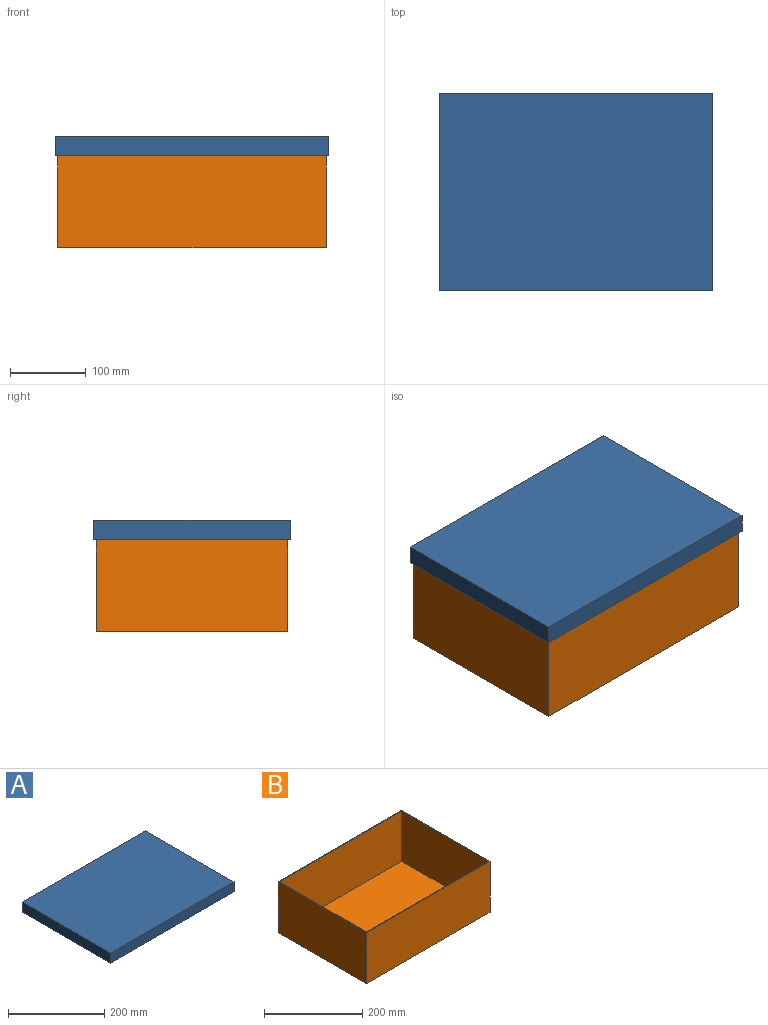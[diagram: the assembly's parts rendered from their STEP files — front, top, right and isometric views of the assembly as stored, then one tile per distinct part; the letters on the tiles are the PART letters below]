
ASSEMBLY  parts=2 mates=1
PART A: 11 faces, bbox 361.6x260x25.4 mm
  f0: plane 357.6x23.42mm, normal (0,1,0), area 8374.6mm2, adj f5,f6,f9,f10
  f1: plane 259.96x25.4mm, normal (1,0,0), area 6603.1mm2, adj f2,f7,f8,f9
  f2: plane 361.56x25.4mm, normal (0,1,0), area 9183.7mm2, adj f1,f3,f8,f9
  f3: plane 259.96x25.4mm, normal (-1,0,0), area 6603.1mm2, adj f2,f7,f8,f9
  f4: plane 357.6x23.42mm, normal (0,-1,0), area 8374.6mm2, adj f5,f6,f9,f10
  f5: plane 256x23.42mm, normal (-1,0,0), area 5995.2mm2, adj f0,f4,f9,f10
  f6: plane 256x23.42mm, normal (1,0,0), area 5995.2mm2, adj f0,f4,f9,f10
  f7: plane 361.56x25.4mm, normal (0,-1,0), area 9183.7mm2, adj f1,f3,f8,f9
  f8: plane 361.56x259.96mm, normal (0,0,1), area 93993.6mm2, adj f1,f2,f3,f7
  f9: plane 361.56x259.96mm, normal (0,0,-1), area 2447mm2, adj f0,f1,f2,f3,f4,f5,f6,f7
  f10: plane 357.6x256mm, normal (0,0,-1), area 91546.5mm2, adj f0,f4,f5,f6
PART B: 11 faces, bbox 355.6x254x127 mm
  f0: plane 351.64x125.02mm, normal (0,-1,0), area 43961.3mm2, adj f1,f6,f8,f10
  f1: plane 250.04x125.02mm, normal (-1,0,0), area 31259.4mm2, adj f0,f2,f8,f10
  f2: plane 351.64x125.02mm, normal (0,1,0), area 43961.3mm2, adj f1,f6,f8,f10
  f3: plane 254x127mm, normal (-1,0,0), area 32258mm2, adj f4,f7,f8,f9
  f4: plane 355.6x127mm, normal (0,-1,0), area 45161.2mm2, adj f3,f5,f8,f9
  f5: plane 254x127mm, normal (1,0,0), area 32258mm2, adj f4,f7,f8,f9
  f6: plane 250.04x125.02mm, normal (1,0,0), area 31259.4mm2, adj f0,f2,f8,f10
  f7: plane 355.6x127mm, normal (0,1,0), area 45161.2mm2, adj f3,f5,f8,f9
  f8: plane 355.6x254mm, normal (0,0,1), area 2399.8mm2, adj f0,f1,f2,f3,f4,f5,f6,f7
  f9: plane 355.6x254mm, normal (0,0,-1), area 90322.4mm2, adj f3,f4,f5,f7
  f10: plane 351.64x250.04mm, normal (0,0,1), area 87922.6mm2, adj f0,f1,f2,f6
PLACE A t=(36.73,39.36,8.28)mm
PLACE B t=(36.73,39.36,0.25)mm fixed
MATE slider A.f10 <-> B.f10  axis (0,0,-1) through (214.53,166.36,146)mm
